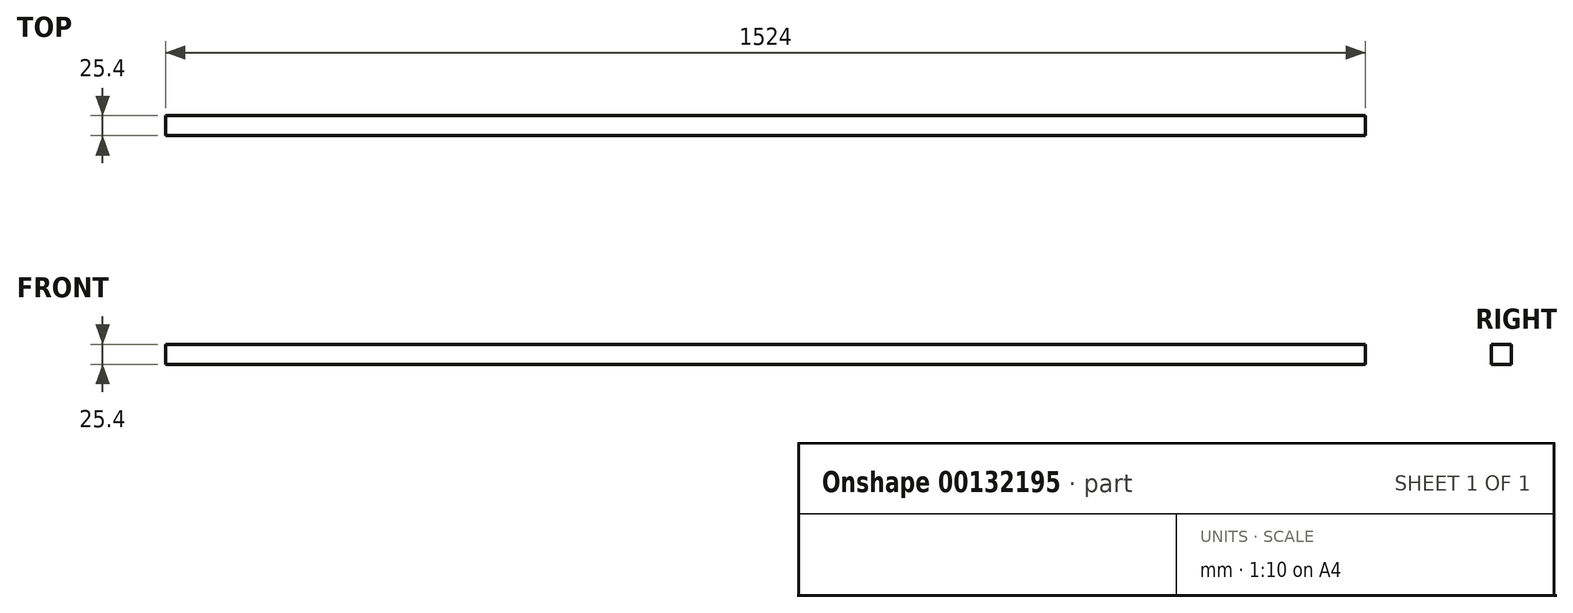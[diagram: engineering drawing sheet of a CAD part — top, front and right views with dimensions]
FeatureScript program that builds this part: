
annotation { "Feature Type Name" : "Feature", "Feature Type Description" : "" }
export const myFeature = defineFeature(function(context is Context, id is Id, definition is map)
    precondition{}
    {
        {
            var Q0;
            Q0=qCreatedBy(makeId("Top.planeOp"),FACE);
            var sketch = newSketch(context, id + "F0", { "sketchPlane" : qUnion([Q0])});
            skLineSegment(sketch, "E0.bottom", {"start": v(0, 0) * mm, "end": v(1524, 0) * mm});
            skLineSegment(sketch, "E0.top", {"start": v(0, 25.4) * mm, "end": v(1524, 25.4) * mm});
            skLineSegment(sketch, "E0.left", {"start": v(0, 0) * mm, "end": v(0, 25.4) * mm});
            skLineSegment(sketch, "E0.right", {"start": v(1524, 0) * mm, "end": v(1524, 25.4) * mm});
            skSolve(sketch);
        }
        {
            var Q0;
            Q0 = qSketchRegion(id + "F0", true);
            extrude(context, id + "F1", {"entities" : qUnion([Q0]), "depth" : 25.4 * mm});
        }
    });
